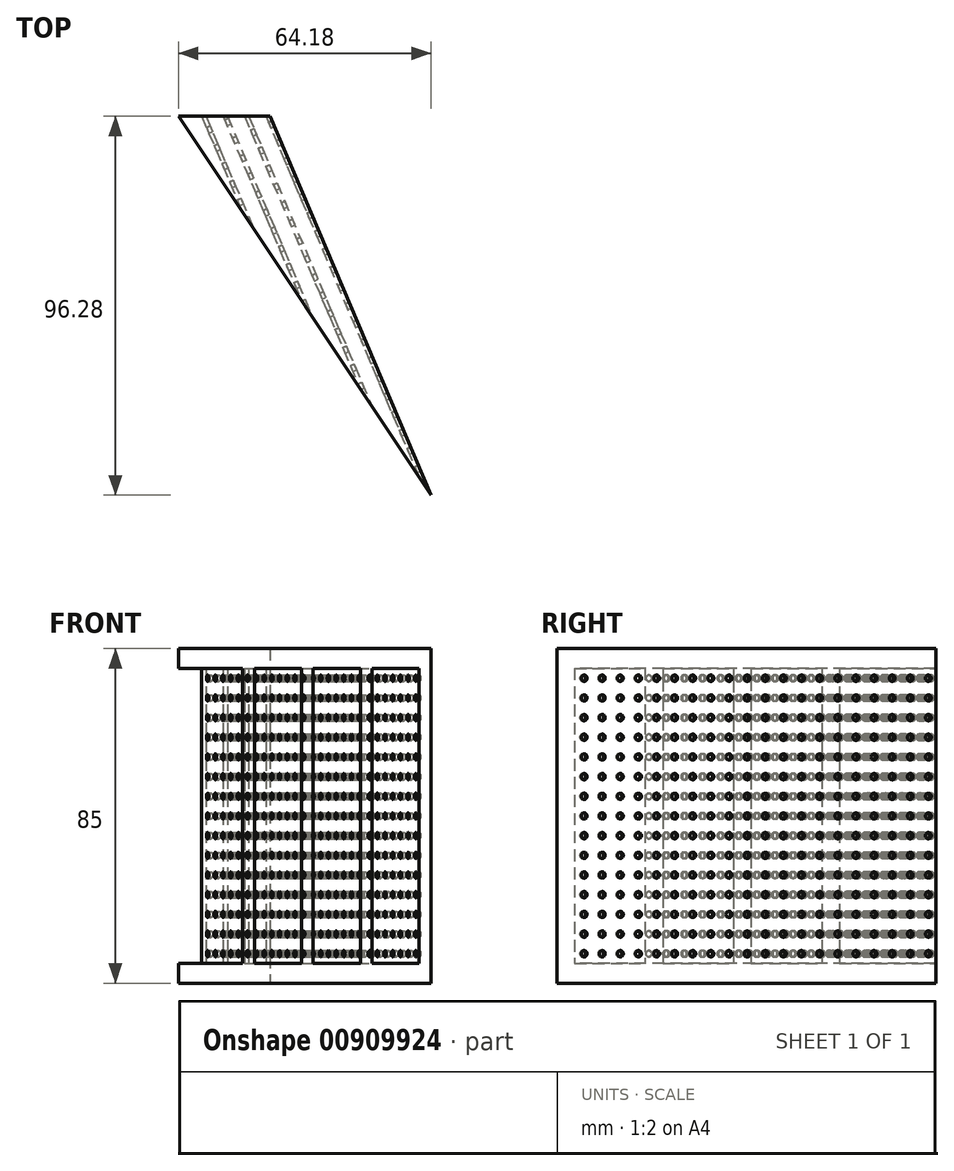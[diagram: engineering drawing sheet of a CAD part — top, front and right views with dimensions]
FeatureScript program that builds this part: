
annotation { "Feature Type Name" : "Feature", "Feature Type Description" : "" }
export const myFeature = defineFeature(function(context is Context, id is Id, definition is map)
    precondition{}
    {
        {
            var Q0;
            Q0=qCreatedBy(makeId("Top.planeOp"),FACE);
            var sketch = newSketch(context, id + "F0", { "sketchPlane" : qUnion([Q0])});
            skLineSegment(sketch, "E0", {"start": v(0, -87) * mm, "end": v(0, 141.6) * mm});
            skLineSegment(sketch, "E1", {"start": v(0, -87) * mm, "end": v(-76.2, 141.6) * mm});
            skLineSegment(sketch, "E2", {"start": v(-76.2, 141.6) * mm, "end": v(0, 141.6) * mm});
            skLineSegment(sketch, "E3", {"start": v(0, -87) * mm, "end": v(-152.4, 141.6) * mm});
            skLineSegment(sketch, "E4", {"start": v(-152.4, 141.6) * mm, "end": v(-76.2, 141.6) * mm});
            skLineSegment(sketch, "E5.3.0.0", {"start": v(-129.63, 141.6) * mm, "end": v(-89.71, 47.57) * mm});
            skLineSegment(sketch, "E5.4.0.0", {"start": v(-135.06, 141.6) * mm, "end": v(-104.66, 70) * mm});
            skLineSegment(sketch, "E5.5.0.0", {"start": v(-140.49, 141.6) * mm, "end": v(-119.61, 92.43) * mm});
            skLineSegment(sketch, "E5.6.0.0", {"start": v(-145.92, 141.6) * mm, "end": v(-134.57, 114.86) * mm});
            skLineSegment(sketch, "E6", {"start": v(-130.17, 141.6) * mm, "end": v(-91.2, 49.82) * mm});
            skLineSegment(sketch, "E7", {"start": v(-129.08, 141.6) * mm, "end": v(-88.22, 45.33) * mm});
            skLineSegment(sketch, "E8", {"start": v(-134.51, 141.6) * mm, "end": v(-103.17, 67.76) * mm});
            skLineSegment(sketch, "E9", {"start": v(-135.6, 141.6) * mm, "end": v(-106.16, 72.24) * mm});
            skLineSegment(sketch, "E10", {"start": v(-141.03, 141.6) * mm, "end": v(-121.1, 94.67) * mm});
            skLineSegment(sketch, "E11", {"start": v(-139.95, 141.6) * mm, "end": v(-118.12, 90.19) * mm});
            skLineSegment(sketch, "E12", {"start": v(-146.46, 141.6) * mm, "end": v(-136.06, 117.1) * mm});
            skLineSegment(sketch, "E13", {"start": v(-145.38, 141.6) * mm, "end": v(-133.07, 112.61) * mm});
            skPoint(sketch, "E14.endSnap0", {"position": v(-70.9, 119.68) * mm});
            skLineSegment(sketch, "E15", {"start": v(-74.88, 141.6) * mm, "end": v(1.19, -86.6) * mm});
            skLineSegment(sketch, "E16", {"start": v(1.19, -86.6) * mm, "end": v(0, -87) * mm});
            skSolve(sketch);
        }
        {
            var Q0;
            {var subQ0=sQuery(id+"F0.wireOp",EDGE,"tio6LvUo-ufc0-BAlz-zotA-NuJ3DqPMcApA");Q0=makeQuery(id+"F0.imprint","IMPRINT",FACE,{"disambiguationData":[TD([[makeQuery(id+"F0.imprint","IMPRINT",EDGE,{"derivedFrom":subQ0}),-1.0]])]});}
            var Q1;
            {var subQ0=sQuery(id+"F0.wireOp",EDGE,"tio6LvUo-ufc0-BAlz-zotA-NuJ3DqPMcApA");Q1=makeQuery(id+"F0.imprint","IMPRINT",FACE,{"disambiguationData":[TD([[makeQuery(id+"F0.imprint","IMPRINT",EDGE,{"derivedFrom":subQ0}),1.0]])]});}
            var Q2;
            {var subQ0=sQuery(id+"F0.wireOp",EDGE,"4e188bdb-a84d-468f-a136-6ee99db43824.2.0.0");Q2=makeQuery(id+"F0.imprint","IMPRINT",FACE,{"disambiguationData":[TD([[makeQuery(id+"F0.imprint","IMPRINT",EDGE,{"derivedFrom":subQ0}),1.0]])]});}
            var Q3;
            {var subQ0=sQuery(id+"F0.wireOp",EDGE,"4e188bdb-a84d-468f-a136-6ee99db43824.2.0.0");Q3=makeQuery(id+"F0.imprint","IMPRINT",FACE,{"disambiguationData":[TD([[makeQuery(id+"F0.imprint","IMPRINT",EDGE,{"derivedFrom":subQ0}),-1.0]])]});}
            var Q4;
            {var subQ0=sQuery(id+"F0.wireOp",EDGE,"4e188bdb-a84d-468f-a136-6ee99db43824.1.0.0");Q4=makeQuery(id+"F0.imprint","IMPRINT",FACE,{"disambiguationData":[TD([[makeQuery(id+"F0.imprint","IMPRINT",EDGE,{"derivedFrom":subQ0}),1.0]])]});}
            var Q5;
            {var subQ0=sQuery(id+"F0.wireOp",EDGE,"4e188bdb-a84d-468f-a136-6ee99db43824.1.0.0");Q5=makeQuery(id+"F0.imprint","IMPRINT",FACE,{"disambiguationData":[TD([[makeQuery(id+"F0.imprint","IMPRINT",EDGE,{"derivedFrom":subQ0}),-1.0]])]});}
            var Q6;
            {var subQ0=sQuery(id+"F0.wireOp",EDGE,"WQDTFHoN-cVkg-57EL-m2Ek-3fZDlS1s6eJM");Q6=makeQuery(id+"F0.imprint","IMPRINT",FACE,{"disambiguationData":[TD([[makeQuery(id+"F0.imprint","IMPRINT",EDGE,{"derivedFrom":subQ0}),1.0]])]});}
            var Q7;
            {var subQ0=sQuery(id+"F0.wireOp",EDGE,"WQDTFHoN-cVkg-57EL-m2Ek-3fZDlS1s6eJM");Q7=makeQuery(id+"F0.imprint","IMPRINT",FACE,{"disambiguationData":[TD([[makeQuery(id+"F0.imprint","IMPRINT",EDGE,{"derivedFrom":subQ0}),-1.0]])]});}
            var Q8;
            {var subQ0=sQuery(id+"F0.wireOp",EDGE,"wjyRamf8-mvhk-V4Mk-rHR7-FkbCW1w5zshC");Q8=makeQuery(id+"F0.imprint","IMPRINT",FACE,{"disambiguationData":[TD([[makeQuery(id+"F0.imprint","IMPRINT",EDGE,{"derivedFrom":subQ0}),1.0]])]});}
            var Q9;
            {var subQ0=sQuery(id+"F0.wireOp",EDGE,"wjyRamf8-mvhk-V4Mk-rHR7-FkbCW1w5zshC");Q9=makeQuery(id+"F0.imprint","IMPRINT",FACE,{"disambiguationData":[TD([[makeQuery(id+"F0.imprint","IMPRINT",EDGE,{"derivedFrom":subQ0}),-1.0]])]});}
            var Q10;
            {var subQ0=sQuery(id+"F0.wireOp",EDGE,"3xIirhRW-c74D-KqQh-bdU1-G7A9PWOAMrXJ");Q10=makeQuery(id+"F0.imprint","IMPRINT",FACE,{"disambiguationData":[TD([[makeQuery(id+"F0.imprint","IMPRINT",EDGE,{"derivedFrom":subQ0}),1.0]])]});}
            var Q11;
            {var subQ0=sQuery(id+"F0.wireOp",EDGE,"3xIirhRW-c74D-KqQh-bdU1-G7A9PWOAMrXJ");Q11=makeQuery(id+"F0.imprint","IMPRINT",FACE,{"disambiguationData":[TD([[makeQuery(id+"F0.imprint","IMPRINT",EDGE,{"derivedFrom":subQ0}),-1.0]])]});}
            var Q12;
            {var subQ0=sQuery(id+"F0.wireOp",EDGE,"Cx8qQpw4-EkkS-4kxI-8c3x-LNEGa1anCedo");Q12=makeQuery(id+"F0.imprint","IMPRINT",FACE,{"disambiguationData":[TD([[makeQuery(id+"F0.imprint","IMPRINT",EDGE,{"derivedFrom":subQ0}),1.0]])]});}
            var Q13;
            {var subQ0=sQuery(id+"F0.wireOp",EDGE,"Cx8qQpw4-EkkS-4kxI-8c3x-LNEGa1anCedo");Q13=makeQuery(id+"F0.imprint","IMPRINT",FACE,{"disambiguationData":[TD([[makeQuery(id+"F0.imprint","IMPRINT",EDGE,{"derivedFrom":subQ0}),-1.0]])]});}
            var Q14;
            {var subQ0=sQuery(id+"F0.wireOp",EDGE,"E5.1.0.0");Q14=makeQuery(id+"F0.imprint","IMPRINT",FACE,{"disambiguationData":[TD([[makeQuery(id+"F0.imprint","IMPRINT",EDGE,{"derivedFrom":subQ0}),1.0]])]});}
            var Q15;
            {var subQ0=sQuery(id+"F0.wireOp",EDGE,"E5.1.0.0");Q15=makeQuery(id+"F0.imprint","IMPRINT",FACE,{"disambiguationData":[TD([[makeQuery(id+"F0.imprint","IMPRINT",EDGE,{"derivedFrom":subQ0}),-1.0]])]});}
            var Q16;
            {var subQ0=sQuery(id+"F0.wireOp",EDGE,"E5.2.0.0");Q16=makeQuery(id+"F0.imprint","IMPRINT",FACE,{"disambiguationData":[TD([[makeQuery(id+"F0.imprint","IMPRINT",EDGE,{"derivedFrom":subQ0}),1.0]])]});}
            var Q17;
            {var subQ0=sQuery(id+"F0.wireOp",EDGE,"E5.2.0.0");Q17=makeQuery(id+"F0.imprint","IMPRINT",FACE,{"disambiguationData":[TD([[makeQuery(id+"F0.imprint","IMPRINT",EDGE,{"derivedFrom":subQ0}),-1.0]])]});}
            var Q18;
            {var subQ0=sQuery(id+"F0.wireOp",EDGE,"E5.3.0.0");Q18=makeQuery(id+"F0.imprint","IMPRINT",FACE,{"disambiguationData":[TD([[makeQuery(id+"F0.imprint","IMPRINT",EDGE,{"derivedFrom":subQ0}),1.0]])]});}
            var Q19;
            {var subQ0=sQuery(id+"F0.wireOp",EDGE,"E5.3.0.0");Q19=makeQuery(id+"F0.imprint","IMPRINT",FACE,{"disambiguationData":[TD([[makeQuery(id+"F0.imprint","IMPRINT",EDGE,{"derivedFrom":subQ0}),-1.0]])]});}
            var Q20;
            {var subQ0=sQuery(id+"F0.wireOp",EDGE,"E5.4.0.0");Q20=makeQuery(id+"F0.imprint","IMPRINT",FACE,{"disambiguationData":[TD([[makeQuery(id+"F0.imprint","IMPRINT",EDGE,{"derivedFrom":subQ0}),1.0]])]});}
            var Q21;
            {var subQ0=sQuery(id+"F0.wireOp",EDGE,"E5.4.0.0");Q21=makeQuery(id+"F0.imprint","IMPRINT",FACE,{"disambiguationData":[TD([[makeQuery(id+"F0.imprint","IMPRINT",EDGE,{"derivedFrom":subQ0}),-1.0]])]});}
            var Q22;
            {var subQ0=sQuery(id+"F0.wireOp",EDGE,"E5.5.0.0");Q22=makeQuery(id+"F0.imprint","IMPRINT",FACE,{"disambiguationData":[TD([[makeQuery(id+"F0.imprint","IMPRINT",EDGE,{"derivedFrom":subQ0}),1.0]])]});}
            var Q23;
            {var subQ0=sQuery(id+"F0.wireOp",EDGE,"E5.5.0.0");Q23=makeQuery(id+"F0.imprint","IMPRINT",FACE,{"disambiguationData":[TD([[makeQuery(id+"F0.imprint","IMPRINT",EDGE,{"derivedFrom":subQ0}),-1.0]])]});}
            var Q24;
            {var subQ0=sQuery(id+"F0.wireOp",EDGE,"E5.6.0.0");Q24=makeQuery(id+"F0.imprint","IMPRINT",FACE,{"disambiguationData":[TD([[makeQuery(id+"F0.imprint","IMPRINT",EDGE,{"derivedFrom":subQ0}),1.0]])]});}
            var Q25;
            {var subQ0=sQuery(id+"F0.wireOp",EDGE,"E5.6.0.0");Q25=makeQuery(id+"F0.imprint","IMPRINT",FACE,{"disambiguationData":[TD([[makeQuery(id+"F0.imprint","IMPRINT",EDGE,{"derivedFrom":subQ0}),-1.0]])]});}
            extrude(context, id + "F1", {"entities" : qUnion([Q0, Q1, Q2, Q3, Q4, Q5, Q6, Q7, Q8, Q9, Q10, Q11, Q12, Q13, Q14, Q15, Q16, Q17, Q18, Q19, Q20, Q21, Q22, Q23, Q24, Q25]), "depth" : 75 * mm, "offsetDistance" : 25 * mm});
        }
        {
            var Q0;
            {var subQ0=sQuery(id+"F0.wireOp",EDGE,"E6");Q0=makeQuery(id+"F0.imprint","IMPRINT",FACE,{"disambiguationData":[TD([[makeQuery(id+"F0.imprint","IMPRINT",EDGE,{"derivedFrom":subQ0}),-1.0]])]});}
            var Q1;
            {var subQ0=sQuery(id+"F0.wireOp",EDGE,"E5.3.0.0");Q1=makeQuery(id+"F0.imprint","IMPRINT",FACE,{"disambiguationData":[TD([[makeQuery(id+"F0.imprint","IMPRINT",EDGE,{"derivedFrom":subQ0}),1.0]])]});}
            var Q2;
            {var subQ0=sQuery(id+"F0.wireOp",EDGE,"E5.3.0.0");Q2=makeQuery(id+"F0.imprint","IMPRINT",FACE,{"disambiguationData":[TD([[makeQuery(id+"F0.imprint","IMPRINT",EDGE,{"derivedFrom":subQ0}),-1.0]])]});}
            var Q3;
            {var subQ0=sQuery(id+"F0.wireOp",EDGE,"E5.4.0.0");Q3=makeQuery(id+"F0.imprint","IMPRINT",FACE,{"disambiguationData":[TD([[makeQuery(id+"F0.imprint","IMPRINT",EDGE,{"derivedFrom":subQ0}),1.0]])]});}
            var Q4;
            {var subQ0=sQuery(id+"F0.wireOp",EDGE,"E5.4.0.0");Q4=makeQuery(id+"F0.imprint","IMPRINT",FACE,{"disambiguationData":[TD([[makeQuery(id+"F0.imprint","IMPRINT",EDGE,{"derivedFrom":subQ0}),-1.0]])]});}
            var Q5;
            {var subQ0=sQuery(id+"F0.wireOp",EDGE,"E9");Q5=makeQuery(id+"F0.imprint","IMPRINT",FACE,{"disambiguationData":[TD([[makeQuery(id+"F0.imprint","IMPRINT",EDGE,{"derivedFrom":subQ0}),-1.0]])]});}
            var Q6;
            {var subQ0=sQuery(id+"F0.wireOp",EDGE,"E10");Q6=makeQuery(id+"F0.imprint","IMPRINT",FACE,{"disambiguationData":[TD([[makeQuery(id+"F0.imprint","IMPRINT",EDGE,{"derivedFrom":subQ0}),-1.0]])]});}
            var Q7;
            {var subQ0=sQuery(id+"F0.wireOp",EDGE,"E5.5.0.0");Q7=makeQuery(id+"F0.imprint","IMPRINT",FACE,{"disambiguationData":[TD([[makeQuery(id+"F0.imprint","IMPRINT",EDGE,{"derivedFrom":subQ0}),-1.0]])]});}
            var Q8;
            {var subQ0=sQuery(id+"F0.wireOp",EDGE,"E5.5.0.0");Q8=makeQuery(id+"F0.imprint","IMPRINT",FACE,{"disambiguationData":[TD([[makeQuery(id+"F0.imprint","IMPRINT",EDGE,{"derivedFrom":subQ0}),1.0]])]});}
            var Q9;
            {var subQ0=sQuery(id+"F0.wireOp",EDGE,"E5.6.0.0");Q9=makeQuery(id+"F0.imprint","IMPRINT",FACE,{"disambiguationData":[TD([[makeQuery(id+"F0.imprint","IMPRINT",EDGE,{"derivedFrom":subQ0}),1.0]])]});}
            var Q10;
            {var subQ0=sQuery(id+"F0.wireOp",EDGE,"E5.6.0.0");Q10=makeQuery(id+"F0.imprint","IMPRINT",FACE,{"disambiguationData":[TD([[makeQuery(id+"F0.imprint","IMPRINT",EDGE,{"derivedFrom":subQ0}),-1.0]])]});}
            var Q11;
            {var subQ3=sQuery(id+"F0.wireOp",EDGE,"E12");Q11=makeQuery(id+"F0.imprint","IMPRINT",FACE,{"disambiguationData":[TD([[makeQuery(id+"F0.imprint","IMPRINT",EDGE,{"derivedFrom":subQ3}),-1.0]])]});}
            extrude(context, id + "F2", {"entities" : qUnion([Q0, Q1, Q2, Q3, Q4, Q5, Q6, Q7, Q8, Q9, Q10, Q11]), "operationType" : NewBodyOperationType.ADD, "oppositeDirection" : true, "depth" : 5 * mm, "offsetDistance" : 25 * mm});
        }
        {
            var Q0;
            Q0=makeQuery(id+"F1.opExtrude","SWEPT_FACE",FACE,{"disambiguationData":[OSD([sQuery(id+"F0.wireOp",EDGE,"E6")])]});
            var sketch = newSketch(context, id + "F3", { "sketchPlane" : qUnion([Q0])});
            skLineSegment(sketch, "E17.left", {"start": v(-181.21, 0) * mm, "end": v(-181.21, 5) * mm});
            skCircle(sketch, "E18", {"center": v(-178.71, 2.5) * mm, "radius": 0.8 * mm});
            skCircle(sketch, "E19.0.1.0", {"center": v(-178.71, 7.5) * mm, "radius": 0.8 * mm});
            skCircle(sketch, "E19.0.2.0", {"center": v(-178.71, 12.5) * mm, "radius": 0.8 * mm});
            skCircle(sketch, "E19.0.3.0", {"center": v(-178.71, 17.5) * mm, "radius": 0.8 * mm});
            skCircle(sketch, "E19.0.4.0", {"center": v(-178.71, 22.5) * mm, "radius": 0.8 * mm});
            skCircle(sketch, "E19.0.5.0", {"center": v(-178.71, 27.5) * mm, "radius": 0.8 * mm});
            skCircle(sketch, "E19.0.6.0", {"center": v(-178.71, 32.5) * mm, "radius": 0.8 * mm});
            skCircle(sketch, "E19.0.7.0", {"center": v(-178.71, 37.5) * mm, "radius": 0.8 * mm});
            skCircle(sketch, "E19.0.8.0", {"center": v(-178.71, 42.5) * mm, "radius": 0.8 * mm});
            skCircle(sketch, "E19.0.9.0", {"center": v(-178.71, 47.5) * mm, "radius": 0.8 * mm});
            skCircle(sketch, "E19.0.10.0", {"center": v(-178.71, 52.5) * mm, "radius": 0.8 * mm});
            skCircle(sketch, "E19.0.11.0", {"center": v(-178.71, 57.5) * mm, "radius": 0.8 * mm});
            skCircle(sketch, "E19.0.12.0", {"center": v(-178.71, 62.5) * mm, "radius": 0.8 * mm});
            skCircle(sketch, "E19.0.13.0", {"center": v(-178.71, 67.5) * mm, "radius": 0.8 * mm});
            skCircle(sketch, "E19.0.14.0", {"center": v(-178.71, 72.5) * mm, "radius": 0.8 * mm});
            skCircle(sketch, "E19.1.0.0", {"center": v(-173.71, 2.5) * mm, "radius": 0.8 * mm});
            skCircle(sketch, "E19.1.1.0", {"center": v(-173.71, 7.5) * mm, "radius": 0.8 * mm});
            skCircle(sketch, "E19.1.2.0", {"center": v(-173.71, 12.5) * mm, "radius": 0.8 * mm});
            skCircle(sketch, "E19.1.3.0", {"center": v(-173.71, 17.5) * mm, "radius": 0.8 * mm});
            skCircle(sketch, "E19.1.4.0", {"center": v(-173.71, 22.5) * mm, "radius": 0.8 * mm});
            skCircle(sketch, "E19.1.5.0", {"center": v(-173.71, 27.5) * mm, "radius": 0.8 * mm});
            skCircle(sketch, "E19.1.6.0", {"center": v(-173.71, 32.5) * mm, "radius": 0.8 * mm});
            skCircle(sketch, "E19.1.7.0", {"center": v(-173.71, 37.5) * mm, "radius": 0.8 * mm});
            skCircle(sketch, "E19.1.8.0", {"center": v(-173.71, 42.5) * mm, "radius": 0.8 * mm});
            skCircle(sketch, "E19.1.9.0", {"center": v(-173.71, 47.5) * mm, "radius": 0.8 * mm});
            skCircle(sketch, "E19.1.10.0", {"center": v(-173.71, 52.5) * mm, "radius": 0.8 * mm});
            skCircle(sketch, "E19.1.11.0", {"center": v(-173.71, 57.5) * mm, "radius": 0.8 * mm});
            skCircle(sketch, "E19.1.12.0", {"center": v(-173.71, 62.5) * mm, "radius": 0.8 * mm});
            skCircle(sketch, "E19.1.13.0", {"center": v(-173.71, 67.5) * mm, "radius": 0.8 * mm});
            skCircle(sketch, "E19.1.14.0", {"center": v(-173.71, 72.5) * mm, "radius": 0.8 * mm});
            skCircle(sketch, "E19.2.0.0", {"center": v(-168.71, 2.5) * mm, "radius": 0.8 * mm});
            skCircle(sketch, "E19.2.1.0", {"center": v(-168.71, 7.5) * mm, "radius": 0.8 * mm});
            skCircle(sketch, "E19.2.2.0", {"center": v(-168.71, 12.5) * mm, "radius": 0.8 * mm});
            skCircle(sketch, "E19.2.3.0", {"center": v(-168.71, 17.5) * mm, "radius": 0.8 * mm});
            skCircle(sketch, "E19.2.4.0", {"center": v(-168.71, 22.5) * mm, "radius": 0.8 * mm});
            skCircle(sketch, "E19.2.5.0", {"center": v(-168.71, 27.5) * mm, "radius": 0.8 * mm});
            skCircle(sketch, "E19.2.6.0", {"center": v(-168.71, 32.5) * mm, "radius": 0.8 * mm});
            skCircle(sketch, "E19.2.7.0", {"center": v(-168.71, 37.5) * mm, "radius": 0.8 * mm});
            skCircle(sketch, "E19.2.8.0", {"center": v(-168.71, 42.5) * mm, "radius": 0.8 * mm});
            skCircle(sketch, "E19.2.9.0", {"center": v(-168.71, 47.5) * mm, "radius": 0.8 * mm});
            skCircle(sketch, "E19.2.10.0", {"center": v(-168.71, 52.5) * mm, "radius": 0.8 * mm});
            skCircle(sketch, "E19.2.11.0", {"center": v(-168.71, 57.5) * mm, "radius": 0.8 * mm});
            skCircle(sketch, "E19.2.12.0", {"center": v(-168.71, 62.5) * mm, "radius": 0.8 * mm});
            skCircle(sketch, "E19.2.13.0", {"center": v(-168.71, 67.5) * mm, "radius": 0.8 * mm});
            skCircle(sketch, "E19.2.14.0", {"center": v(-168.71, 72.5) * mm, "radius": 0.8 * mm});
            skCircle(sketch, "E19.3.0.0", {"center": v(-163.71, 2.5) * mm, "radius": 0.8 * mm});
            skCircle(sketch, "E19.3.1.0", {"center": v(-163.71, 7.5) * mm, "radius": 0.8 * mm});
            skCircle(sketch, "E19.3.2.0", {"center": v(-163.71, 12.5) * mm, "radius": 0.8 * mm});
            skCircle(sketch, "E19.3.3.0", {"center": v(-163.71, 17.5) * mm, "radius": 0.8 * mm});
            skCircle(sketch, "E19.3.4.0", {"center": v(-163.71, 22.5) * mm, "radius": 0.8 * mm});
            skCircle(sketch, "E19.3.5.0", {"center": v(-163.71, 27.5) * mm, "radius": 0.8 * mm});
            skCircle(sketch, "E19.3.6.0", {"center": v(-163.71, 32.5) * mm, "radius": 0.8 * mm});
            skCircle(sketch, "E19.3.7.0", {"center": v(-163.71, 37.5) * mm, "radius": 0.8 * mm});
            skCircle(sketch, "E19.3.8.0", {"center": v(-163.71, 42.5) * mm, "radius": 0.8 * mm});
            skCircle(sketch, "E19.3.9.0", {"center": v(-163.71, 47.5) * mm, "radius": 0.8 * mm});
            skCircle(sketch, "E19.3.10.0", {"center": v(-163.71, 52.5) * mm, "radius": 0.8 * mm});
            skCircle(sketch, "E19.3.11.0", {"center": v(-163.71, 57.5) * mm, "radius": 0.8 * mm});
            skCircle(sketch, "E19.3.12.0", {"center": v(-163.71, 62.5) * mm, "radius": 0.8 * mm});
            skCircle(sketch, "E19.3.13.0", {"center": v(-163.71, 67.5) * mm, "radius": 0.8 * mm});
            skCircle(sketch, "E19.3.14.0", {"center": v(-163.71, 72.5) * mm, "radius": 0.8 * mm});
            skCircle(sketch, "E19.4.0.0", {"center": v(-158.71, 2.5) * mm, "radius": 0.8 * mm});
            skCircle(sketch, "E19.4.1.0", {"center": v(-158.71, 7.5) * mm, "radius": 0.8 * mm});
            skCircle(sketch, "E19.4.2.0", {"center": v(-158.71, 12.5) * mm, "radius": 0.8 * mm});
            skCircle(sketch, "E19.4.3.0", {"center": v(-158.71, 17.5) * mm, "radius": 0.8 * mm});
            skCircle(sketch, "E19.4.4.0", {"center": v(-158.71, 22.5) * mm, "radius": 0.8 * mm});
            skCircle(sketch, "E19.4.5.0", {"center": v(-158.71, 27.5) * mm, "radius": 0.8 * mm});
            skCircle(sketch, "E19.4.6.0", {"center": v(-158.71, 32.5) * mm, "radius": 0.8 * mm});
            skCircle(sketch, "E19.4.7.0", {"center": v(-158.71, 37.5) * mm, "radius": 0.8 * mm});
            skCircle(sketch, "E19.4.8.0", {"center": v(-158.71, 42.5) * mm, "radius": 0.8 * mm});
            skCircle(sketch, "E19.4.9.0", {"center": v(-158.71, 47.5) * mm, "radius": 0.8 * mm});
            skCircle(sketch, "E19.4.10.0", {"center": v(-158.71, 52.5) * mm, "radius": 0.8 * mm});
            skCircle(sketch, "E19.4.11.0", {"center": v(-158.71, 57.5) * mm, "radius": 0.8 * mm});
            skCircle(sketch, "E19.4.12.0", {"center": v(-158.71, 62.5) * mm, "radius": 0.8 * mm});
            skCircle(sketch, "E19.4.13.0", {"center": v(-158.71, 67.5) * mm, "radius": 0.8 * mm});
            skCircle(sketch, "E19.4.14.0", {"center": v(-158.71, 72.5) * mm, "radius": 0.8 * mm});
            skCircle(sketch, "E19.5.0.0", {"center": v(-153.71, 2.5) * mm, "radius": 0.8 * mm});
            skCircle(sketch, "E19.5.1.0", {"center": v(-153.71, 7.5) * mm, "radius": 0.8 * mm});
            skCircle(sketch, "E19.5.2.0", {"center": v(-153.71, 12.5) * mm, "radius": 0.8 * mm});
            skCircle(sketch, "E19.5.3.0", {"center": v(-153.71, 17.5) * mm, "radius": 0.8 * mm});
            skCircle(sketch, "E19.5.4.0", {"center": v(-153.71, 22.5) * mm, "radius": 0.8 * mm});
            skCircle(sketch, "E19.5.5.0", {"center": v(-153.71, 27.5) * mm, "radius": 0.8 * mm});
            skCircle(sketch, "E19.5.6.0", {"center": v(-153.71, 32.5) * mm, "radius": 0.8 * mm});
            skCircle(sketch, "E19.5.7.0", {"center": v(-153.71, 37.5) * mm, "radius": 0.8 * mm});
            skCircle(sketch, "E19.5.8.0", {"center": v(-153.71, 42.5) * mm, "radius": 0.8 * mm});
            skCircle(sketch, "E19.5.9.0", {"center": v(-153.71, 47.5) * mm, "radius": 0.8 * mm});
            skCircle(sketch, "E19.5.10.0", {"center": v(-153.71, 52.5) * mm, "radius": 0.8 * mm});
            skCircle(sketch, "E19.5.11.0", {"center": v(-153.71, 57.5) * mm, "radius": 0.8 * mm});
            skCircle(sketch, "E19.5.12.0", {"center": v(-153.71, 62.5) * mm, "radius": 0.8 * mm});
            skCircle(sketch, "E19.5.13.0", {"center": v(-153.71, 67.5) * mm, "radius": 0.8 * mm});
            skCircle(sketch, "E19.5.14.0", {"center": v(-153.71, 72.5) * mm, "radius": 0.8 * mm});
            skCircle(sketch, "E19.6.0.0", {"center": v(-148.71, 2.5) * mm, "radius": 0.8 * mm});
            skCircle(sketch, "E19.6.1.0", {"center": v(-148.71, 7.5) * mm, "radius": 0.8 * mm});
            skCircle(sketch, "E19.6.2.0", {"center": v(-148.71, 12.5) * mm, "radius": 0.8 * mm});
            skCircle(sketch, "E19.6.3.0", {"center": v(-148.71, 17.5) * mm, "radius": 0.8 * mm});
            skCircle(sketch, "E19.6.4.0", {"center": v(-148.71, 22.5) * mm, "radius": 0.8 * mm});
            skCircle(sketch, "E19.6.5.0", {"center": v(-148.71, 27.5) * mm, "radius": 0.8 * mm});
            skCircle(sketch, "E19.6.6.0", {"center": v(-148.71, 32.5) * mm, "radius": 0.8 * mm});
            skCircle(sketch, "E19.6.7.0", {"center": v(-148.71, 37.5) * mm, "radius": 0.8 * mm});
            skCircle(sketch, "E19.6.8.0", {"center": v(-148.71, 42.5) * mm, "radius": 0.8 * mm});
            skCircle(sketch, "E19.6.9.0", {"center": v(-148.71, 47.5) * mm, "radius": 0.8 * mm});
            skCircle(sketch, "E19.6.10.0", {"center": v(-148.71, 52.5) * mm, "radius": 0.8 * mm});
            skCircle(sketch, "E19.6.11.0", {"center": v(-148.71, 57.5) * mm, "radius": 0.8 * mm});
            skCircle(sketch, "E19.6.12.0", {"center": v(-148.71, 62.5) * mm, "radius": 0.8 * mm});
            skCircle(sketch, "E19.6.13.0", {"center": v(-148.71, 67.5) * mm, "radius": 0.8 * mm});
            skCircle(sketch, "E19.6.14.0", {"center": v(-148.71, 72.5) * mm, "radius": 0.8 * mm});
            skCircle(sketch, "E19.7.0.0", {"center": v(-143.71, 2.5) * mm, "radius": 0.8 * mm});
            skCircle(sketch, "E19.7.1.0", {"center": v(-143.71, 7.5) * mm, "radius": 0.8 * mm});
            skCircle(sketch, "E19.7.2.0", {"center": v(-143.71, 12.5) * mm, "radius": 0.8 * mm});
            skCircle(sketch, "E19.7.3.0", {"center": v(-143.71, 17.5) * mm, "radius": 0.8 * mm});
            skCircle(sketch, "E19.7.4.0", {"center": v(-143.71, 22.5) * mm, "radius": 0.8 * mm});
            skCircle(sketch, "E19.7.5.0", {"center": v(-143.71, 27.5) * mm, "radius": 0.8 * mm});
            skCircle(sketch, "E19.7.6.0", {"center": v(-143.71, 32.5) * mm, "radius": 0.8 * mm});
            skCircle(sketch, "E19.7.7.0", {"center": v(-143.71, 37.5) * mm, "radius": 0.8 * mm});
            skCircle(sketch, "E19.7.8.0", {"center": v(-143.71, 42.5) * mm, "radius": 0.8 * mm});
            skCircle(sketch, "E19.7.9.0", {"center": v(-143.71, 47.5) * mm, "radius": 0.8 * mm});
            skCircle(sketch, "E19.7.10.0", {"center": v(-143.71, 52.5) * mm, "radius": 0.8 * mm});
            skCircle(sketch, "E19.7.11.0", {"center": v(-143.71, 57.5) * mm, "radius": 0.8 * mm});
            skCircle(sketch, "E19.7.12.0", {"center": v(-143.71, 62.5) * mm, "radius": 0.8 * mm});
            skCircle(sketch, "E19.7.13.0", {"center": v(-143.71, 67.5) * mm, "radius": 0.8 * mm});
            skCircle(sketch, "E19.7.14.0", {"center": v(-143.71, 72.5) * mm, "radius": 0.8 * mm});
            skCircle(sketch, "E19.8.0.0", {"center": v(-138.71, 2.5) * mm, "radius": 0.8 * mm});
            skCircle(sketch, "E19.8.1.0", {"center": v(-138.71, 7.5) * mm, "radius": 0.8 * mm});
            skCircle(sketch, "E19.8.2.0", {"center": v(-138.71, 12.5) * mm, "radius": 0.8 * mm});
            skCircle(sketch, "E19.8.3.0", {"center": v(-138.71, 17.5) * mm, "radius": 0.8 * mm});
            skCircle(sketch, "E19.8.4.0", {"center": v(-138.71, 22.5) * mm, "radius": 0.8 * mm});
            skCircle(sketch, "E19.8.5.0", {"center": v(-138.71, 27.5) * mm, "radius": 0.8 * mm});
            skCircle(sketch, "E19.8.6.0", {"center": v(-138.71, 32.5) * mm, "radius": 0.8 * mm});
            skCircle(sketch, "E19.8.7.0", {"center": v(-138.71, 37.5) * mm, "radius": 0.8 * mm});
            skCircle(sketch, "E19.8.8.0", {"center": v(-138.71, 42.5) * mm, "radius": 0.8 * mm});
            skCircle(sketch, "E19.8.9.0", {"center": v(-138.71, 47.5) * mm, "radius": 0.8 * mm});
            skCircle(sketch, "E19.8.10.0", {"center": v(-138.71, 52.5) * mm, "radius": 0.8 * mm});
            skCircle(sketch, "E19.8.11.0", {"center": v(-138.71, 57.5) * mm, "radius": 0.8 * mm});
            skCircle(sketch, "E19.8.12.0", {"center": v(-138.71, 62.5) * mm, "radius": 0.8 * mm});
            skCircle(sketch, "E19.8.13.0", {"center": v(-138.71, 67.5) * mm, "radius": 0.8 * mm});
            skCircle(sketch, "E19.8.14.0", {"center": v(-138.71, 72.5) * mm, "radius": 0.8 * mm});
            skCircle(sketch, "E19.9.0.0", {"center": v(-133.71, 2.5) * mm, "radius": 0.8 * mm});
            skCircle(sketch, "E19.9.1.0", {"center": v(-133.71, 7.5) * mm, "radius": 0.8 * mm});
            skCircle(sketch, "E19.9.2.0", {"center": v(-133.71, 12.5) * mm, "radius": 0.8 * mm});
            skCircle(sketch, "E19.9.3.0", {"center": v(-133.71, 17.5) * mm, "radius": 0.8 * mm});
            skCircle(sketch, "E19.9.4.0", {"center": v(-133.71, 22.5) * mm, "radius": 0.8 * mm});
            skCircle(sketch, "E19.9.5.0", {"center": v(-133.71, 27.5) * mm, "radius": 0.8 * mm});
            skCircle(sketch, "E19.9.6.0", {"center": v(-133.71, 32.5) * mm, "radius": 0.8 * mm});
            skCircle(sketch, "E19.9.7.0", {"center": v(-133.71, 37.5) * mm, "radius": 0.8 * mm});
            skCircle(sketch, "E19.9.8.0", {"center": v(-133.71, 42.5) * mm, "radius": 0.8 * mm});
            skCircle(sketch, "E19.9.9.0", {"center": v(-133.71, 47.5) * mm, "radius": 0.8 * mm});
            skCircle(sketch, "E19.9.10.0", {"center": v(-133.71, 52.5) * mm, "radius": 0.8 * mm});
            skCircle(sketch, "E19.9.11.0", {"center": v(-133.71, 57.5) * mm, "radius": 0.8 * mm});
            skCircle(sketch, "E19.9.12.0", {"center": v(-133.71, 62.5) * mm, "radius": 0.8 * mm});
            skCircle(sketch, "E19.9.13.0", {"center": v(-133.71, 67.5) * mm, "radius": 0.8 * mm});
            skCircle(sketch, "E19.9.14.0", {"center": v(-133.71, 72.5) * mm, "radius": 0.8 * mm});
            skCircle(sketch, "E19.10.0.0", {"center": v(-128.71, 2.5) * mm, "radius": 0.8 * mm});
            skCircle(sketch, "E19.10.1.0", {"center": v(-128.71, 7.5) * mm, "radius": 0.8 * mm});
            skCircle(sketch, "E19.10.2.0", {"center": v(-128.71, 12.5) * mm, "radius": 0.8 * mm});
            skCircle(sketch, "E19.10.3.0", {"center": v(-128.71, 17.5) * mm, "radius": 0.8 * mm});
            skCircle(sketch, "E19.10.4.0", {"center": v(-128.71, 22.5) * mm, "radius": 0.8 * mm});
            skCircle(sketch, "E19.10.5.0", {"center": v(-128.71, 27.5) * mm, "radius": 0.8 * mm});
            skCircle(sketch, "E19.10.6.0", {"center": v(-128.71, 32.5) * mm, "radius": 0.8 * mm});
            skCircle(sketch, "E19.10.7.0", {"center": v(-128.71, 37.5) * mm, "radius": 0.8 * mm});
            skCircle(sketch, "E19.10.8.0", {"center": v(-128.71, 42.5) * mm, "radius": 0.8 * mm});
            skCircle(sketch, "E19.10.9.0", {"center": v(-128.71, 47.5) * mm, "radius": 0.8 * mm});
            skCircle(sketch, "E19.10.10.0", {"center": v(-128.71, 52.5) * mm, "radius": 0.8 * mm});
            skCircle(sketch, "E19.10.11.0", {"center": v(-128.71, 57.5) * mm, "radius": 0.8 * mm});
            skCircle(sketch, "E19.10.12.0", {"center": v(-128.71, 62.5) * mm, "radius": 0.8 * mm});
            skCircle(sketch, "E19.10.13.0", {"center": v(-128.71, 67.5) * mm, "radius": 0.8 * mm});
            skCircle(sketch, "E19.10.14.0", {"center": v(-128.71, 72.5) * mm, "radius": 0.8 * mm});
            skCircle(sketch, "E19.11.0.0", {"center": v(-123.71, 2.5) * mm, "radius": 0.8 * mm});
            skCircle(sketch, "E19.11.1.0", {"center": v(-123.71, 7.5) * mm, "radius": 0.8 * mm});
            skCircle(sketch, "E19.11.2.0", {"center": v(-123.71, 12.5) * mm, "radius": 0.8 * mm});
            skCircle(sketch, "E19.11.3.0", {"center": v(-123.71, 17.5) * mm, "radius": 0.8 * mm});
            skCircle(sketch, "E19.11.4.0", {"center": v(-123.71, 22.5) * mm, "radius": 0.8 * mm});
            skCircle(sketch, "E19.11.5.0", {"center": v(-123.71, 27.5) * mm, "radius": 0.8 * mm});
            skCircle(sketch, "E19.11.6.0", {"center": v(-123.71, 32.5) * mm, "radius": 0.8 * mm});
            skCircle(sketch, "E19.11.7.0", {"center": v(-123.71, 37.5) * mm, "radius": 0.8 * mm});
            skCircle(sketch, "E19.11.8.0", {"center": v(-123.71, 42.5) * mm, "radius": 0.8 * mm});
            skCircle(sketch, "E19.11.9.0", {"center": v(-123.71, 47.5) * mm, "radius": 0.8 * mm});
            skCircle(sketch, "E19.11.10.0", {"center": v(-123.71, 52.5) * mm, "radius": 0.8 * mm});
            skCircle(sketch, "E19.11.11.0", {"center": v(-123.71, 57.5) * mm, "radius": 0.8 * mm});
            skCircle(sketch, "E19.11.12.0", {"center": v(-123.71, 62.5) * mm, "radius": 0.8 * mm});
            skCircle(sketch, "E19.11.13.0", {"center": v(-123.71, 67.5) * mm, "radius": 0.8 * mm});
            skCircle(sketch, "E19.11.14.0", {"center": v(-123.71, 72.5) * mm, "radius": 0.8 * mm});
            skCircle(sketch, "E19.12.0.0", {"center": v(-118.71, 2.5) * mm, "radius": 0.8 * mm});
            skCircle(sketch, "E19.12.1.0", {"center": v(-118.71, 7.5) * mm, "radius": 0.8 * mm});
            skCircle(sketch, "E19.12.2.0", {"center": v(-118.71, 12.5) * mm, "radius": 0.8 * mm});
            skCircle(sketch, "E19.12.3.0", {"center": v(-118.71, 17.5) * mm, "radius": 0.8 * mm});
            skCircle(sketch, "E19.12.4.0", {"center": v(-118.71, 22.5) * mm, "radius": 0.8 * mm});
            skCircle(sketch, "E19.12.5.0", {"center": v(-118.71, 27.5) * mm, "radius": 0.8 * mm});
            skCircle(sketch, "E19.12.6.0", {"center": v(-118.71, 32.5) * mm, "radius": 0.8 * mm});
            skCircle(sketch, "E19.12.7.0", {"center": v(-118.71, 37.5) * mm, "radius": 0.8 * mm});
            skCircle(sketch, "E19.12.8.0", {"center": v(-118.71, 42.5) * mm, "radius": 0.8 * mm});
            skCircle(sketch, "E19.12.9.0", {"center": v(-118.71, 47.5) * mm, "radius": 0.8 * mm});
            skCircle(sketch, "E19.12.10.0", {"center": v(-118.71, 52.5) * mm, "radius": 0.8 * mm});
            skCircle(sketch, "E19.12.11.0", {"center": v(-118.71, 57.5) * mm, "radius": 0.8 * mm});
            skCircle(sketch, "E19.12.12.0", {"center": v(-118.71, 62.5) * mm, "radius": 0.8 * mm});
            skCircle(sketch, "E19.12.13.0", {"center": v(-118.71, 67.5) * mm, "radius": 0.8 * mm});
            skCircle(sketch, "E19.12.14.0", {"center": v(-118.71, 72.5) * mm, "radius": 0.8 * mm});
            skCircle(sketch, "E19.13.0.0", {"center": v(-113.71, 2.5) * mm, "radius": 0.8 * mm});
            skCircle(sketch, "E19.13.1.0", {"center": v(-113.71, 7.5) * mm, "radius": 0.8 * mm});
            skCircle(sketch, "E19.13.2.0", {"center": v(-113.71, 12.5) * mm, "radius": 0.8 * mm});
            skCircle(sketch, "E19.13.3.0", {"center": v(-113.71, 17.5) * mm, "radius": 0.8 * mm});
            skCircle(sketch, "E19.13.4.0", {"center": v(-113.71, 22.5) * mm, "radius": 0.8 * mm});
            skCircle(sketch, "E19.13.5.0", {"center": v(-113.71, 27.5) * mm, "radius": 0.8 * mm});
            skCircle(sketch, "E19.13.6.0", {"center": v(-113.71, 32.5) * mm, "radius": 0.8 * mm});
            skCircle(sketch, "E19.13.7.0", {"center": v(-113.71, 37.5) * mm, "radius": 0.8 * mm});
            skCircle(sketch, "E19.13.8.0", {"center": v(-113.71, 42.5) * mm, "radius": 0.8 * mm});
            skCircle(sketch, "E19.13.9.0", {"center": v(-113.71, 47.5) * mm, "radius": 0.8 * mm});
            skCircle(sketch, "E19.13.10.0", {"center": v(-113.71, 52.5) * mm, "radius": 0.8 * mm});
            skCircle(sketch, "E19.13.11.0", {"center": v(-113.71, 57.5) * mm, "radius": 0.8 * mm});
            skCircle(sketch, "E19.13.12.0", {"center": v(-113.71, 62.5) * mm, "radius": 0.8 * mm});
            skCircle(sketch, "E19.13.13.0", {"center": v(-113.71, 67.5) * mm, "radius": 0.8 * mm});
            skCircle(sketch, "E19.13.14.0", {"center": v(-113.71, 72.5) * mm, "radius": 0.8 * mm});
            skCircle(sketch, "E19.14.0.0", {"center": v(-108.71, 2.5) * mm, "radius": 0.8 * mm});
            skCircle(sketch, "E19.14.1.0", {"center": v(-108.71, 7.5) * mm, "radius": 0.8 * mm});
            skCircle(sketch, "E19.14.2.0", {"center": v(-108.71, 12.5) * mm, "radius": 0.8 * mm});
            skCircle(sketch, "E19.14.3.0", {"center": v(-108.71, 17.5) * mm, "radius": 0.8 * mm});
            skCircle(sketch, "E19.14.4.0", {"center": v(-108.71, 22.5) * mm, "radius": 0.8 * mm});
            skCircle(sketch, "E19.14.5.0", {"center": v(-108.71, 27.5) * mm, "radius": 0.8 * mm});
            skCircle(sketch, "E19.14.6.0", {"center": v(-108.71, 32.5) * mm, "radius": 0.8 * mm});
            skCircle(sketch, "E19.14.7.0", {"center": v(-108.71, 37.5) * mm, "radius": 0.8 * mm});
            skCircle(sketch, "E19.14.8.0", {"center": v(-108.71, 42.5) * mm, "radius": 0.8 * mm});
            skCircle(sketch, "E19.14.9.0", {"center": v(-108.71, 47.5) * mm, "radius": 0.8 * mm});
            skCircle(sketch, "E19.14.10.0", {"center": v(-108.71, 52.5) * mm, "radius": 0.8 * mm});
            skCircle(sketch, "E19.14.11.0", {"center": v(-108.71, 57.5) * mm, "radius": 0.8 * mm});
            skCircle(sketch, "E19.14.12.0", {"center": v(-108.71, 62.5) * mm, "radius": 0.8 * mm});
            skCircle(sketch, "E19.14.13.0", {"center": v(-108.71, 67.5) * mm, "radius": 0.8 * mm});
            skCircle(sketch, "E19.14.14.0", {"center": v(-108.71, 72.5) * mm, "radius": 0.8 * mm});
            skCircle(sketch, "E19.15.0.0", {"center": v(-103.71, 2.5) * mm, "radius": 0.8 * mm});
            skCircle(sketch, "E19.15.1.0", {"center": v(-103.71, 7.5) * mm, "radius": 0.8 * mm});
            skCircle(sketch, "E19.15.2.0", {"center": v(-103.71, 12.5) * mm, "radius": 0.8 * mm});
            skCircle(sketch, "E19.15.3.0", {"center": v(-103.71, 17.5) * mm, "radius": 0.8 * mm});
            skCircle(sketch, "E19.15.4.0", {"center": v(-103.71, 22.5) * mm, "radius": 0.8 * mm});
            skCircle(sketch, "E19.15.5.0", {"center": v(-103.71, 27.5) * mm, "radius": 0.8 * mm});
            skCircle(sketch, "E19.15.6.0", {"center": v(-103.71, 32.5) * mm, "radius": 0.8 * mm});
            skCircle(sketch, "E19.15.7.0", {"center": v(-103.71, 37.5) * mm, "radius": 0.8 * mm});
            skCircle(sketch, "E19.15.8.0", {"center": v(-103.71, 42.5) * mm, "radius": 0.8 * mm});
            skCircle(sketch, "E19.15.9.0", {"center": v(-103.71, 47.5) * mm, "radius": 0.8 * mm});
            skCircle(sketch, "E19.15.10.0", {"center": v(-103.71, 52.5) * mm, "radius": 0.8 * mm});
            skCircle(sketch, "E19.15.11.0", {"center": v(-103.71, 57.5) * mm, "radius": 0.8 * mm});
            skCircle(sketch, "E19.15.12.0", {"center": v(-103.71, 62.5) * mm, "radius": 0.8 * mm});
            skCircle(sketch, "E19.15.13.0", {"center": v(-103.71, 67.5) * mm, "radius": 0.8 * mm});
            skCircle(sketch, "E19.15.14.0", {"center": v(-103.71, 72.5) * mm, "radius": 0.8 * mm});
            skCircle(sketch, "E19.16.0.0", {"center": v(-98.71, 2.5) * mm, "radius": 0.8 * mm});
            skCircle(sketch, "E19.16.1.0", {"center": v(-98.71, 7.5) * mm, "radius": 0.8 * mm});
            skCircle(sketch, "E19.16.2.0", {"center": v(-98.71, 12.5) * mm, "radius": 0.8 * mm});
            skCircle(sketch, "E19.16.3.0", {"center": v(-98.71, 17.5) * mm, "radius": 0.8 * mm});
            skCircle(sketch, "E19.16.4.0", {"center": v(-98.71, 22.5) * mm, "radius": 0.8 * mm});
            skCircle(sketch, "E19.16.5.0", {"center": v(-98.71, 27.5) * mm, "radius": 0.8 * mm});
            skCircle(sketch, "E19.16.6.0", {"center": v(-98.71, 32.5) * mm, "radius": 0.8 * mm});
            skCircle(sketch, "E19.16.7.0", {"center": v(-98.71, 37.5) * mm, "radius": 0.8 * mm});
            skCircle(sketch, "E19.16.8.0", {"center": v(-98.71, 42.5) * mm, "radius": 0.8 * mm});
            skCircle(sketch, "E19.16.9.0", {"center": v(-98.71, 47.5) * mm, "radius": 0.8 * mm});
            skCircle(sketch, "E19.16.10.0", {"center": v(-98.71, 52.5) * mm, "radius": 0.8 * mm});
            skCircle(sketch, "E19.16.11.0", {"center": v(-98.71, 57.5) * mm, "radius": 0.8 * mm});
            skCircle(sketch, "E19.16.12.0", {"center": v(-98.71, 62.5) * mm, "radius": 0.8 * mm});
            skCircle(sketch, "E19.16.13.0", {"center": v(-98.71, 67.5) * mm, "radius": 0.8 * mm});
            skCircle(sketch, "E19.16.14.0", {"center": v(-98.71, 72.5) * mm, "radius": 0.8 * mm});
            skCircle(sketch, "E19.17.0.0", {"center": v(-93.71, 2.5) * mm, "radius": 0.8 * mm});
            skCircle(sketch, "E19.17.1.0", {"center": v(-93.71, 7.5) * mm, "radius": 0.8 * mm});
            skCircle(sketch, "E19.17.2.0", {"center": v(-93.71, 12.5) * mm, "radius": 0.8 * mm});
            skCircle(sketch, "E19.17.3.0", {"center": v(-93.71, 17.5) * mm, "radius": 0.8 * mm});
            skCircle(sketch, "E19.17.4.0", {"center": v(-93.71, 22.5) * mm, "radius": 0.8 * mm});
            skCircle(sketch, "E19.17.5.0", {"center": v(-93.71, 27.5) * mm, "radius": 0.8 * mm});
            skCircle(sketch, "E19.17.6.0", {"center": v(-93.71, 32.5) * mm, "radius": 0.8 * mm});
            skCircle(sketch, "E19.17.7.0", {"center": v(-93.71, 37.5) * mm, "radius": 0.8 * mm});
            skCircle(sketch, "E19.17.8.0", {"center": v(-93.71, 42.5) * mm, "radius": 0.8 * mm});
            skCircle(sketch, "E19.17.9.0", {"center": v(-93.71, 47.5) * mm, "radius": 0.8 * mm});
            skCircle(sketch, "E19.17.10.0", {"center": v(-93.71, 52.5) * mm, "radius": 0.8 * mm});
            skCircle(sketch, "E19.17.11.0", {"center": v(-93.71, 57.5) * mm, "radius": 0.8 * mm});
            skCircle(sketch, "E19.17.12.0", {"center": v(-93.71, 62.5) * mm, "radius": 0.8 * mm});
            skCircle(sketch, "E19.17.13.0", {"center": v(-93.71, 67.5) * mm, "radius": 0.8 * mm});
            skCircle(sketch, "E19.17.14.0", {"center": v(-93.71, 72.5) * mm, "radius": 0.8 * mm});
            skCircle(sketch, "E19.18.0.0", {"center": v(-88.71, 2.5) * mm, "radius": 0.8 * mm});
            skCircle(sketch, "E19.18.1.0", {"center": v(-88.71, 7.5) * mm, "radius": 0.8 * mm});
            skCircle(sketch, "E19.18.2.0", {"center": v(-88.71, 12.5) * mm, "radius": 0.8 * mm});
            skCircle(sketch, "E19.18.3.0", {"center": v(-88.71, 17.5) * mm, "radius": 0.8 * mm});
            skCircle(sketch, "E19.18.4.0", {"center": v(-88.71, 22.5) * mm, "radius": 0.8 * mm});
            skCircle(sketch, "E19.18.5.0", {"center": v(-88.71, 27.5) * mm, "radius": 0.8 * mm});
            skCircle(sketch, "E19.18.6.0", {"center": v(-88.71, 32.5) * mm, "radius": 0.8 * mm});
            skCircle(sketch, "E19.18.7.0", {"center": v(-88.71, 37.5) * mm, "radius": 0.8 * mm});
            skCircle(sketch, "E19.18.8.0", {"center": v(-88.71, 42.5) * mm, "radius": 0.8 * mm});
            skCircle(sketch, "E19.18.9.0", {"center": v(-88.71, 47.5) * mm, "radius": 0.8 * mm});
            skCircle(sketch, "E19.18.10.0", {"center": v(-88.71, 52.5) * mm, "radius": 0.8 * mm});
            skCircle(sketch, "E19.18.11.0", {"center": v(-88.71, 57.5) * mm, "radius": 0.8 * mm});
            skCircle(sketch, "E19.18.12.0", {"center": v(-88.71, 62.5) * mm, "radius": 0.8 * mm});
            skCircle(sketch, "E19.18.13.0", {"center": v(-88.71, 67.5) * mm, "radius": 0.8 * mm});
            skCircle(sketch, "E19.18.14.0", {"center": v(-88.71, 72.5) * mm, "radius": 0.8 * mm});
            skCircle(sketch, "E19.19.0.0", {"center": v(-83.71, 2.5) * mm, "radius": 0.8 * mm});
            skCircle(sketch, "E19.19.1.0", {"center": v(-83.71, 7.5) * mm, "radius": 0.8 * mm});
            skCircle(sketch, "E19.19.2.0", {"center": v(-83.71, 12.5) * mm, "radius": 0.8 * mm});
            skCircle(sketch, "E19.19.3.0", {"center": v(-83.71, 17.5) * mm, "radius": 0.8 * mm});
            skCircle(sketch, "E19.19.4.0", {"center": v(-83.71, 22.5) * mm, "radius": 0.8 * mm});
            skCircle(sketch, "E19.19.5.0", {"center": v(-83.71, 27.5) * mm, "radius": 0.8 * mm});
            skCircle(sketch, "E19.19.6.0", {"center": v(-83.71, 32.5) * mm, "radius": 0.8 * mm});
            skCircle(sketch, "E19.19.7.0", {"center": v(-83.71, 37.5) * mm, "radius": 0.8 * mm});
            skCircle(sketch, "E19.19.8.0", {"center": v(-83.71, 42.5) * mm, "radius": 0.8 * mm});
            skCircle(sketch, "E19.19.9.0", {"center": v(-83.71, 47.5) * mm, "radius": 0.8 * mm});
            skCircle(sketch, "E19.19.10.0", {"center": v(-83.71, 52.5) * mm, "radius": 0.8 * mm});
            skCircle(sketch, "E19.19.11.0", {"center": v(-83.71, 57.5) * mm, "radius": 0.8 * mm});
            skCircle(sketch, "E19.19.12.0", {"center": v(-83.71, 62.5) * mm, "radius": 0.8 * mm});
            skCircle(sketch, "E19.19.13.0", {"center": v(-83.71, 67.5) * mm, "radius": 0.8 * mm});
            skCircle(sketch, "E19.19.14.0", {"center": v(-83.71, 72.5) * mm, "radius": 0.8 * mm});
            skLineSegment(sketch, "E19.direction1", {"start": v(-178.71, 2.5) * mm, "end": v(-173.71, 2.5) * mm, "construction": true});
            skLineSegment(sketch, "E19.direction2", {"start": v(-178.71, 2.5) * mm, "end": v(-178.71, 7.5) * mm, "construction": true});
            skCircle(sketch, "E20.1.0.0", {"center": v(-183.71, 72.5) * mm, "radius": 0.8 * mm});
            skCircle(sketch, "E20.1.1.0", {"center": v(-183.71, 67.5) * mm, "radius": 0.8 * mm});
            skCircle(sketch, "E20.1.2.0", {"center": v(-183.71, 62.5) * mm, "radius": 0.8 * mm});
            skCircle(sketch, "E20.1.3.0", {"center": v(-183.71, 57.5) * mm, "radius": 0.8 * mm});
            skCircle(sketch, "E20.1.4.0", {"center": v(-183.71, 52.5) * mm, "radius": 0.8 * mm});
            skCircle(sketch, "E20.1.5.0", {"center": v(-183.71, 47.5) * mm, "radius": 0.8 * mm});
            skCircle(sketch, "E20.1.6.0", {"center": v(-183.71, 42.5) * mm, "radius": 0.8 * mm});
            skCircle(sketch, "E20.1.7.0", {"center": v(-183.71, 37.5) * mm, "radius": 0.8 * mm});
            skCircle(sketch, "E20.1.8.0", {"center": v(-183.71, 32.5) * mm, "radius": 0.8 * mm});
            skCircle(sketch, "E20.1.9.0", {"center": v(-183.71, 27.5) * mm, "radius": 0.8 * mm});
            skCircle(sketch, "E20.1.10.0", {"center": v(-183.71, 22.5) * mm, "radius": 0.8 * mm});
            skCircle(sketch, "E20.1.11.0", {"center": v(-183.71, 17.5) * mm, "radius": 0.8 * mm});
            skCircle(sketch, "E20.1.12.0", {"center": v(-183.71, 12.5) * mm, "radius": 0.8 * mm});
            skCircle(sketch, "E20.1.13.0", {"center": v(-183.71, 7.5) * mm, "radius": 0.8 * mm});
            skCircle(sketch, "E20.1.14.0", {"center": v(-183.71, 2.5) * mm, "radius": 0.8 * mm});
            skCircle(sketch, "E20.2.0.0", {"center": v(-188.71, 72.5) * mm, "radius": 0.8 * mm});
            skCircle(sketch, "E20.2.1.0", {"center": v(-188.71, 67.5) * mm, "radius": 0.8 * mm});
            skCircle(sketch, "E20.2.2.0", {"center": v(-188.71, 62.5) * mm, "radius": 0.8 * mm});
            skCircle(sketch, "E20.2.3.0", {"center": v(-188.71, 57.5) * mm, "radius": 0.8 * mm});
            skCircle(sketch, "E20.2.4.0", {"center": v(-188.71, 52.5) * mm, "radius": 0.8 * mm});
            skCircle(sketch, "E20.2.5.0", {"center": v(-188.71, 47.5) * mm, "radius": 0.8 * mm});
            skCircle(sketch, "E20.2.6.0", {"center": v(-188.71, 42.5) * mm, "radius": 0.8 * mm});
            skCircle(sketch, "E20.2.7.0", {"center": v(-188.71, 37.5) * mm, "radius": 0.8 * mm});
            skCircle(sketch, "E20.2.8.0", {"center": v(-188.71, 32.5) * mm, "radius": 0.8 * mm});
            skCircle(sketch, "E20.2.9.0", {"center": v(-188.71, 27.5) * mm, "radius": 0.8 * mm});
            skCircle(sketch, "E20.2.10.0", {"center": v(-188.71, 22.5) * mm, "radius": 0.8 * mm});
            skCircle(sketch, "E20.2.11.0", {"center": v(-188.71, 17.5) * mm, "radius": 0.8 * mm});
            skCircle(sketch, "E20.2.12.0", {"center": v(-188.71, 12.5) * mm, "radius": 0.8 * mm});
            skCircle(sketch, "E20.2.13.0", {"center": v(-188.71, 7.5) * mm, "radius": 0.8 * mm});
            skCircle(sketch, "E20.2.14.0", {"center": v(-188.71, 2.5) * mm, "radius": 0.8 * mm});
            skCircle(sketch, "E20.3.0.0", {"center": v(-193.71, 72.5) * mm, "radius": 0.8 * mm});
            skCircle(sketch, "E20.3.1.0", {"center": v(-193.71, 67.5) * mm, "radius": 0.8 * mm});
            skCircle(sketch, "E20.3.2.0", {"center": v(-193.71, 62.5) * mm, "radius": 0.8 * mm});
            skCircle(sketch, "E20.3.3.0", {"center": v(-193.71, 57.5) * mm, "radius": 0.8 * mm});
            skCircle(sketch, "E20.3.4.0", {"center": v(-193.71, 52.5) * mm, "radius": 0.8 * mm});
            skCircle(sketch, "E20.3.5.0", {"center": v(-193.71, 47.5) * mm, "radius": 0.8 * mm});
            skCircle(sketch, "E20.3.6.0", {"center": v(-193.71, 42.5) * mm, "radius": 0.8 * mm});
            skCircle(sketch, "E20.3.7.0", {"center": v(-193.71, 37.5) * mm, "radius": 0.8 * mm});
            skCircle(sketch, "E20.3.8.0", {"center": v(-193.71, 32.5) * mm, "radius": 0.8 * mm});
            skCircle(sketch, "E20.3.9.0", {"center": v(-193.71, 27.5) * mm, "radius": 0.8 * mm});
            skCircle(sketch, "E20.3.10.0", {"center": v(-193.71, 22.5) * mm, "radius": 0.8 * mm});
            skCircle(sketch, "E20.3.11.0", {"center": v(-193.71, 17.5) * mm, "radius": 0.8 * mm});
            skCircle(sketch, "E20.3.12.0", {"center": v(-193.71, 12.5) * mm, "radius": 0.8 * mm});
            skCircle(sketch, "E20.3.13.0", {"center": v(-193.71, 7.5) * mm, "radius": 0.8 * mm});
            skCircle(sketch, "E20.3.14.0", {"center": v(-193.71, 2.5) * mm, "radius": 0.8 * mm});
            skCircle(sketch, "E20.4.0.0", {"center": v(-198.71, 72.5) * mm, "radius": 0.8 * mm});
            skCircle(sketch, "E20.4.1.0", {"center": v(-198.71, 67.5) * mm, "radius": 0.8 * mm});
            skCircle(sketch, "E20.4.2.0", {"center": v(-198.71, 62.5) * mm, "radius": 0.8 * mm});
            skCircle(sketch, "E20.4.3.0", {"center": v(-198.71, 57.5) * mm, "radius": 0.8 * mm});
            skCircle(sketch, "E20.4.4.0", {"center": v(-198.71, 52.5) * mm, "radius": 0.8 * mm});
            skCircle(sketch, "E20.4.5.0", {"center": v(-198.71, 47.5) * mm, "radius": 0.8 * mm});
            skCircle(sketch, "E20.4.6.0", {"center": v(-198.71, 42.5) * mm, "radius": 0.8 * mm});
            skCircle(sketch, "E20.4.7.0", {"center": v(-198.71, 37.5) * mm, "radius": 0.8 * mm});
            skCircle(sketch, "E20.4.8.0", {"center": v(-198.71, 32.5) * mm, "radius": 0.8 * mm});
            skCircle(sketch, "E20.4.9.0", {"center": v(-198.71, 27.5) * mm, "radius": 0.8 * mm});
            skCircle(sketch, "E20.4.10.0", {"center": v(-198.71, 22.5) * mm, "radius": 0.8 * mm});
            skCircle(sketch, "E20.4.11.0", {"center": v(-198.71, 17.5) * mm, "radius": 0.8 * mm});
            skCircle(sketch, "E20.4.12.0", {"center": v(-198.71, 12.5) * mm, "radius": 0.8 * mm});
            skCircle(sketch, "E20.4.13.0", {"center": v(-198.71, 7.5) * mm, "radius": 0.8 * mm});
            skCircle(sketch, "E20.4.14.0", {"center": v(-198.71, 2.5) * mm, "radius": 0.8 * mm});
            skLineSegment(sketch, "E20.direction1", {"start": v(-178.71, 72.5) * mm, "end": v(-183.71, 72.5) * mm, "construction": true});
            skLineSegment(sketch, "E20.direction2", {"start": v(-178.71, 72.5) * mm, "end": v(-178.71, 67.5) * mm, "construction": true});
            skSolve(sketch);
        }
        {
            var Q0;
            Q0 = qSketchRegion(id + "F3", true);
            extrude(context, id + "F4", {"entities" : qUnion([Q0]), "operationType" : NewBodyOperationType.REMOVE, "depth" : 17.9 * mm, "offsetDistance" : 25 * mm, "hasSecondDirection" : true, "secondDirectionOppositeDirection" : true, "secondDirectionDepth" : 4.1 * mm});
        }
        {
            var Q0;
            {var subQ0=sQuery(id+"F0.wireOp",EDGE,"E6");Q0=makeQuery(id+"F0.imprint","IMPRINT",FACE,{"disambiguationData":[TD([[makeQuery(id+"F0.imprint","IMPRINT",EDGE,{"derivedFrom":subQ0}),-1.0]])]});}
            var Q1;
            {var subQ0=sQuery(id+"F0.wireOp",EDGE,"E5.3.0.0");Q1=makeQuery(id+"F0.imprint","IMPRINT",FACE,{"disambiguationData":[TD([[makeQuery(id+"F0.imprint","IMPRINT",EDGE,{"derivedFrom":subQ0}),-1.0]])]});}
            var Q2;
            {var subQ0=sQuery(id+"F0.wireOp",EDGE,"E5.3.0.0");Q2=makeQuery(id+"F0.imprint","IMPRINT",FACE,{"disambiguationData":[TD([[makeQuery(id+"F0.imprint","IMPRINT",EDGE,{"derivedFrom":subQ0}),1.0]])]});}
            var Q3;
            {var subQ0=sQuery(id+"F0.wireOp",EDGE,"E5.4.0.0");Q3=makeQuery(id+"F0.imprint","IMPRINT",FACE,{"disambiguationData":[TD([[makeQuery(id+"F0.imprint","IMPRINT",EDGE,{"derivedFrom":subQ0}),-1.0]])]});}
            var Q4;
            {var subQ0=sQuery(id+"F0.wireOp",EDGE,"E5.4.0.0");Q4=makeQuery(id+"F0.imprint","IMPRINT",FACE,{"disambiguationData":[TD([[makeQuery(id+"F0.imprint","IMPRINT",EDGE,{"derivedFrom":subQ0}),1.0]])]});}
            var Q5;
            {var subQ3=sQuery(id+"F0.wireOp",EDGE,"E12");Q5=makeQuery(id+"F0.imprint","IMPRINT",FACE,{"disambiguationData":[TD([[makeQuery(id+"F0.imprint","IMPRINT",EDGE,{"derivedFrom":subQ3}),-1.0]])]});}
            var Q6;
            {var subQ0=sQuery(id+"F0.wireOp",EDGE,"E9");Q6=makeQuery(id+"F0.imprint","IMPRINT",FACE,{"disambiguationData":[TD([[makeQuery(id+"F0.imprint","IMPRINT",EDGE,{"derivedFrom":subQ0}),-1.0]])]});}
            var Q7;
            {var subQ0=sQuery(id+"F0.wireOp",EDGE,"E10");Q7=makeQuery(id+"F0.imprint","IMPRINT",FACE,{"disambiguationData":[TD([[makeQuery(id+"F0.imprint","IMPRINT",EDGE,{"derivedFrom":subQ0}),-1.0]])]});}
            var Q8;
            {var subQ0=sQuery(id+"F0.wireOp",EDGE,"E5.5.0.0");Q8=makeQuery(id+"F0.imprint","IMPRINT",FACE,{"disambiguationData":[TD([[makeQuery(id+"F0.imprint","IMPRINT",EDGE,{"derivedFrom":subQ0}),-1.0]])]});}
            var Q9;
            {var subQ0=sQuery(id+"F0.wireOp",EDGE,"E5.5.0.0");Q9=makeQuery(id+"F0.imprint","IMPRINT",FACE,{"disambiguationData":[TD([[makeQuery(id+"F0.imprint","IMPRINT",EDGE,{"derivedFrom":subQ0}),1.0]])]});}
            var Q10;
            {var subQ0=sQuery(id+"F0.wireOp",EDGE,"E5.6.0.0");Q10=makeQuery(id+"F0.imprint","IMPRINT",FACE,{"disambiguationData":[TD([[makeQuery(id+"F0.imprint","IMPRINT",EDGE,{"derivedFrom":subQ0}),1.0]])]});}
            var Q11;
            {var subQ0=sQuery(id+"F0.wireOp",EDGE,"E5.6.0.0");Q11=makeQuery(id+"F0.imprint","IMPRINT",FACE,{"disambiguationData":[TD([[makeQuery(id+"F0.imprint","IMPRINT",EDGE,{"derivedFrom":subQ0}),-1.0]])]});}
            extrude(context, id + "F5", {"entities" : qUnion([Q0, Q1, Q2, Q3, Q4, Q5, Q6, Q7, Q8, Q9, Q10, Q11]), "operationType" : NewBodyOperationType.ADD, "depth" : 80 * mm, "offsetDistance" : 25 * mm, "hasSecondDirection" : true, "secondDirectionOppositeDirection" : true, "secondDirectionDepth" : -75 * mm});
        }
    });
